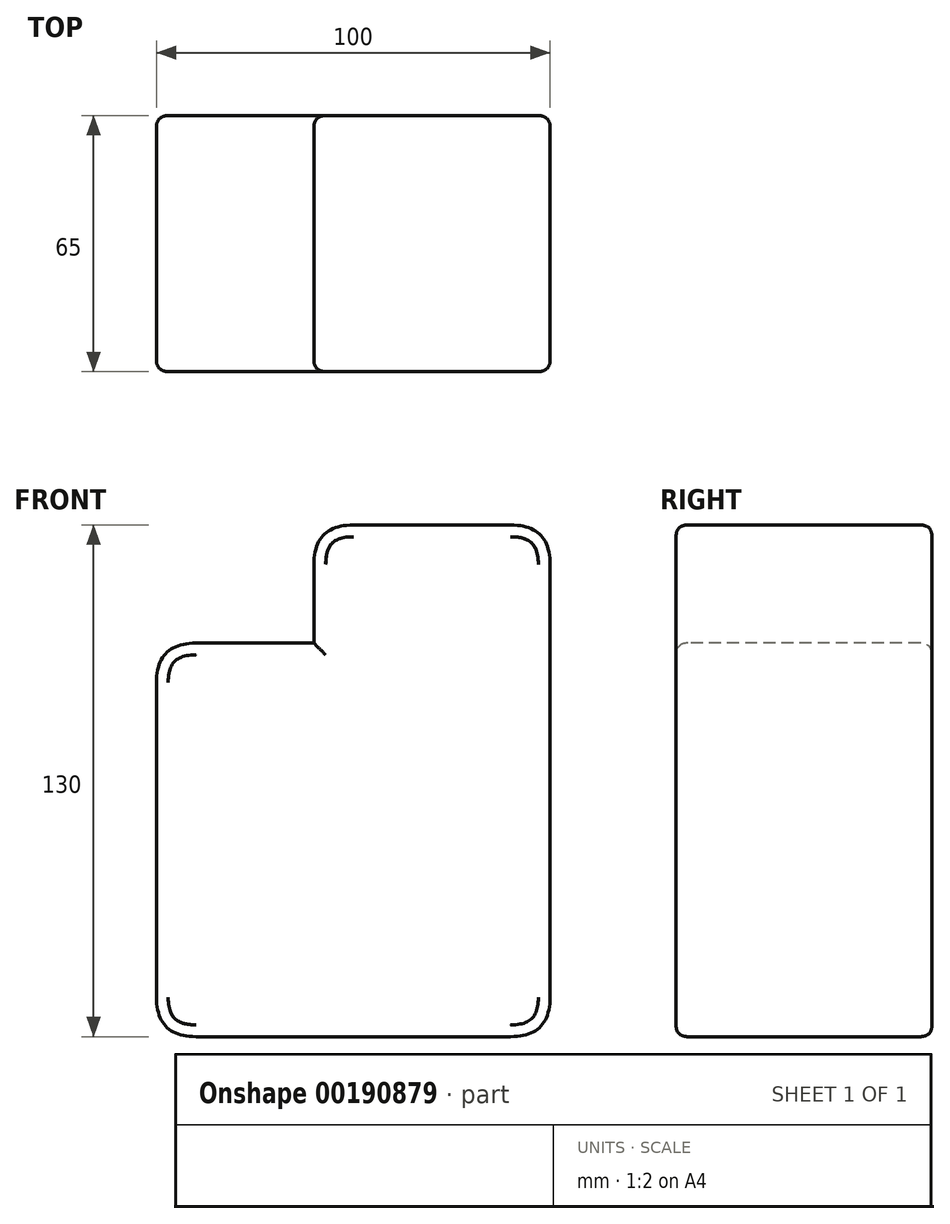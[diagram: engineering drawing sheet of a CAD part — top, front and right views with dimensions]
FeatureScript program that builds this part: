
annotation { "Feature Type Name" : "Feature", "Feature Type Description" : "" }
export const myFeature = defineFeature(function(context is Context, id is Id, definition is map)
    precondition{}
    {
        {
            var Q0;
            Q0=qCreatedBy(makeId("Front.planeOp"),FACE);
            var sketch = newSketch(context, id + "F0", { "sketchPlane" : qUnion([Q0])});
            skLineSegment(sketch, "E0.bottom", {"start": v(50, 50) * mm, "end": v(-50, 50) * mm});
            skLineSegment(sketch, "E0.top", {"start": v(50, -50) * mm, "end": v(-50, -50) * mm});
            skLineSegment(sketch, "E0.left", {"start": v(50, 50) * mm, "end": v(50, -50) * mm});
            skLineSegment(sketch, "E0.right", {"start": v(-50, 50) * mm, "end": v(-50, -50) * mm});
            skPoint(sketch, "E0.middle", {"position": v(0, 0) * mm});
            skSolve(sketch);
        }
        {
            var Q0;
            Q0 = qSketchRegion(id + "F0", true);
            extrude(context, id + "F1", {"entities" : qUnion([Q0]), "depth" : 65 * mm, "symmetric" : true});
        }
        {
            var Q0;
            Q0=makeQuery(id+"F1.opExtrude","SWEPT_FACE",FACE,{"disambiguationData":[OSD([sQuery(id+"F0.wireOp",EDGE,"E0.bottom")])]});
            var sketch = newSketch(context, id + "F2", { "sketchPlane" : qUnion([Q0])});
            skLineSegment(sketch, "E1", {"start": v(-10, 32.5) * mm, "end": v(-10, -32.5) * mm});
            skSolve(sketch);
        }
        {
            var Q0;
            {var subQ0=sQuery(id+"F2.wireOp",EDGE,"E1");Q0=makeQuery(id+"F2.imprint","IMPRINT",FACE,{"disambiguationData":[TD([[makeQuery(id+"F2.imprint","IMPRINT",EDGE,{"derivedFrom":subQ0}),1.0]])]});}
            extrude(context, id + "F3", {"entities" : qUnion([Q0]), "operationType" : NewBodyOperationType.ADD, "depth" : 30 * mm});
        }
        {
            var Q0;
            Q0=makeQuery(id+"F1.opExtrude","SWEPT_EDGE",EDGE,{"disambiguationData":[OSD([sQuery(id+"F0.wireOp",EDGE,"E0.bottom"),sQuery(id+"F0.wireOp",EDGE,"E0.right")])]});
            var Q1;
            Q1=makeQuery(id+"F1.opExtrude","SWEPT_EDGE",EDGE,{"disambiguationData":[OSD([sQuery(id+"F0.wireOp",EDGE,"E0.top"),sQuery(id+"F0.wireOp",EDGE,"E0.right")])]});
            var Q2;
            Q2=makeQuery(id+"F1.opExtrude","SWEPT_EDGE",EDGE,{"disambiguationData":[OSD([sQuery(id+"F0.wireOp",EDGE,"E0.top"),sQuery(id+"F0.wireOp",EDGE,"E0.left")])]});
            var Q3;
            Q3=makeQuery(id+"F3.opExtrude","CAP_EDGE",EDGE,{"disambiguationData":[OSD([sQuery(id+"F0.wireOp",EDGE,"E0.bottom"),sQuery(id+"F0.wireOp",EDGE,"E0.left")])],"isStart":false});
            var Q4;
            Q4=makeQuery(id+"F3.opExtrude","CAP_EDGE",EDGE,{"disambiguationData":[OSD([sQuery(id+"F2.wireOp",EDGE,"E1")])],"isStart":false});
            var Q5;
            Q5=makeQuery(id+"F3.opExtrude","CAP_EDGE",EDGE,{"disambiguationData":[OSD([sQuery(id+"F2.wireOp",EDGE,"E1")])],"isStart":true});
            fillet(context, id + "F4", {"entities" : qUnion([Q0, Q1, Q2, Q3, Q4, Q5]), "radius" : 10 * mm, "tangentPropagation" : true, "rho" : 0.5, "crossSection" : FilletCrossSection.CONIC, "allowEdgeOverflow" : false});
        }
        {
            var Q0;
            {var subQ0=sQuery(id+"F0.wireOp",EDGE,"E0.bottom");var subQ1=makeQuery(id+"F1.opExtrude","CAP_EDGE",EDGE,{"disambiguationData":[OSD([subQ0])],"isStart":false});Q0=makeQuery(id+"F3.opExtrude","CAP_EDGE",EDGE,{"disambiguationData":[OSD([subQ0]),TDD([makeQuery(id+"F2.imprint","IMPRINT",EDGE,{"disambiguationData":[TD([[makeQuery(id+"F2.imprint","INTERSECT",VERTEX,{"derivedFrom":[subQ1,sQuery(id+"F2.wireOp",EDGE,"E1")]}),1.0]])],"derivedFrom":subQ1})])],"isStart":false});}
            var Q1;
            {var subQ0=sQuery(id+"F0.wireOp",EDGE,"E0.bottom");var subQ1=makeQuery(id+"F1.opExtrude","CAP_EDGE",EDGE,{"disambiguationData":[OSD([subQ0])],"isStart":true});Q1=makeQuery(id+"F3.opExtrude","CAP_EDGE",EDGE,{"disambiguationData":[OSD([subQ0]),TDD([makeQuery(id+"F2.imprint","IMPRINT",EDGE,{"disambiguationData":[TD([[makeQuery(id+"F2.imprint","INTERSECT",VERTEX,{"derivedFrom":[subQ1,sQuery(id+"F2.wireOp",EDGE,"E1")]}),1.0]])],"derivedFrom":subQ1})])],"isStart":false});}
            fillet(context, id + "F5", {"entities" : qUnion([Q0, Q1]), "radius" : 3 * mm, "tangentPropagation" : true, "rho" : 0.5, "crossSection" : FilletCrossSection.CONIC, "allowEdgeOverflow" : false});
        }
    });
